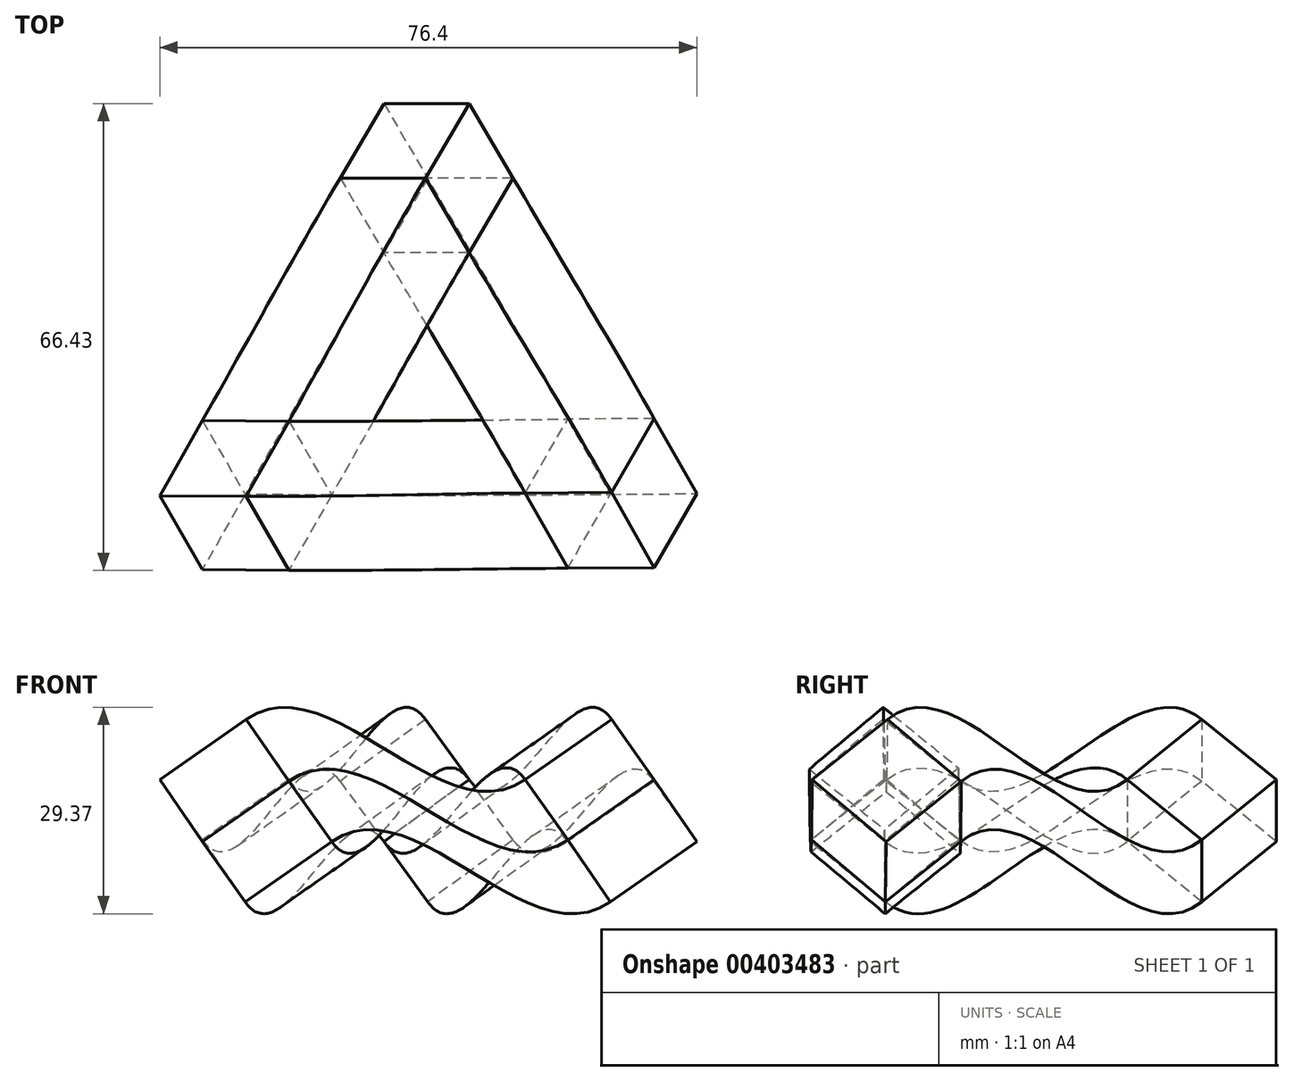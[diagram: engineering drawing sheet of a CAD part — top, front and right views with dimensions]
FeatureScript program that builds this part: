
annotation { "Feature Type Name" : "Feature", "Feature Type Description" : "" }
export const myFeature = defineFeature(function(context is Context, id is Id, definition is map)
    precondition{}
    {
        {
            var Q0;
            Q0=qCreatedBy(makeId("Top.planeOp"),FACE);
            var sketch = newSketch(context, id + "F0", { "sketchPlane" : qUnion([Q0])});
            skLineSegment(sketch, "E0", {"start": v(0, 0) * mm, "end": v(0, 80) * mm, "construction": true});
            skLineSegment(sketch, "E1", {"start": v(0, 0) * mm, "end": v(69.28, -40) * mm, "construction": true});
            skLineSegment(sketch, "E2", {"start": v(0, 0) * mm, "end": v(-69.28, -40) * mm, "construction": true});
            skSolve(sketch);
        }
        {
            var Q0;
            Q0=sQuery(id+"F0.wireOp",EDGE,"E0");
            cPlane(context, id + "F1", {"entities" : qUnion([Q0]), "cplaneType" : CPlaneType.LINE_ANGLE, "offset" : 25 * mm, "angle" : 54 * degree, "width" : 150 * mm, "height" : 150 * mm});
        }
        {
            var Q0;
            Q0=qCreatedBy(id+"F1.planeOp",FACE);
            var sketch = newSketch(context, id + "F2", { "sketchPlane" : qUnion([Q0])});
            skLineSegment(sketch, "E3.top", {"start": v(30, 0) * mm, "end": v(19.4, 10.6) * mm});
            skLineSegment(sketch, "E3.left", {"start": v(40.6, 10.6) * mm, "end": v(30, 0) * mm});
            skLineSegment(sketch, "E3.right", {"start": v(30, 21.21) * mm, "end": v(19.4, 10.6) * mm});
            skLineSegment(sketch, "E4", {"start": v(40.6, 10.6) * mm, "end": v(30, 21.21) * mm});
            skSolve(sketch);
        }
        {
            var Q0;
            Q0=sQuery(id+"F0.wireOp",EDGE,"E2");
            cPlane(context, id + "F3", {"entities" : qUnion([Q0]), "cplaneType" : CPlaneType.LINE_ANGLE, "offset" : 25 * mm, "angle" : 36 * degree, "oppositeDirection" : true, "width" : 150 * mm, "height" : 150 * mm});
        }
        {
            var Q0;
            Q0=qCreatedBy(id+"F3.planeOp",FACE);
            var sketch = newSketch(context, id + "F4", { "sketchPlane" : qUnion([Q0])});
            skLineSegment(sketch, "E5.0", {"start": v(0, 0) * mm, "end": v(-75.76, 25.7) * mm, "construction": true});
            skLineSegment(sketch, "E6", {"start": v(-14.96, 16.28) * mm, "end": v(-28.4, 9.64) * mm});
            skLineSegment(sketch, "E7", {"start": v(-14.96, 16.28) * mm, "end": v(-21.6, 29.73) * mm});
            skLineSegment(sketch, "E8", {"start": v(-35.04, 23.1) * mm, "end": v(-21.6, 29.73) * mm});
            skLineSegment(sketch, "E9", {"start": v(-28.4, 9.64) * mm, "end": v(-35.04, 23.1) * mm});
            skSolve(sketch);
        }
        {
            var Q0;
            Q0=sQuery(id+"F0.wireOp",EDGE,"E1");
            cPlane(context, id + "F5", {"entities" : qUnion([Q0]), "cplaneType" : CPlaneType.LINE_ANGLE, "offset" : 25 * mm, "angle" : 36 * degree, "oppositeDirection" : true, "width" : 150 * mm, "height" : 150 * mm});
        }
        {
            var Q0;
            Q0=qCreatedBy(id+"F5.planeOp",FACE);
            var sketch = newSketch(context, id + "F6", { "sketchPlane" : qUnion([Q0])});
            skLineSegment(sketch, "E10.0", {"start": v(0, 0) * mm, "end": v(-75.76, -25.7) * mm, "construction": true});
            skLineSegment(sketch, "E11", {"start": v(-28.4, -9.64) * mm, "end": v(-41.86, -3) * mm});
            skLineSegment(sketch, "E12", {"start": v(-41.86, -3) * mm, "end": v(-35.23, 10.45) * mm});
            skLineSegment(sketch, "E13", {"start": v(-35.23, 10.45) * mm, "end": v(-21.77, 3.81) * mm});
            skLineSegment(sketch, "E14", {"start": v(-21.77, 3.81) * mm, "end": v(-28.4, -9.64) * mm});
            skSolve(sketch);
        }
        {
            var Q0;
            Q0=makeQuery(id+"F2.imprint","IMPRINT",FACE,{"disambiguationData":[TD([[makeQuery(id+"F2.imprint","IMPRINT",EDGE,{"derivedFrom":sQuery(id+"F2.wireOp",EDGE,"E3.top")}),-1.0]])]});
            extrude(context, id + "F7", {"entities" : qUnion([Q0]), "depth" : 15 * mm});
        }
        {
            var Q0;
            Q0=makeQuery(id+"F4.imprint","IMPRINT",FACE,{"disambiguationData":[TD([[makeQuery(id+"F4.imprint","IMPRINT",EDGE,{"derivedFrom":sQuery(id+"F4.wireOp",EDGE,"E6")}),-1.0]])]});
            extrude(context, id + "F8", {"entities" : qUnion([Q0]), "oppositeDirection" : true, "depth" : 15 * mm});
        }
        {
            var Q0;
            Q0=makeQuery(id+"F6.imprint","IMPRINT",FACE,{"disambiguationData":[TD([[makeQuery(id+"F6.imprint","IMPRINT",EDGE,{"derivedFrom":sQuery(id+"F6.wireOp",EDGE,"E11")}),-1.0]])]});
            extrude(context, id + "F9", {"entities" : qUnion([Q0]), "oppositeDirection" : true, "depth" : 15 * mm});
        }
        {
            var Q0;
            Q0=makeQuery(id+"F7.opExtrude","SWEPT_FACE",FACE,{"disambiguationData":[OSD([sQuery(id+"F2.wireOp",EDGE,"E3.right")])]});
            var Q1;
            Q1=makeQuery(id+"F8.opExtrude","SWEPT_FACE",FACE,{"disambiguationData":[OSD([sQuery(id+"F4.wireOp",EDGE,"E6")])]});
            loft(context, id + "F10", {"startCondition" : LoftEndDerivativeType.NORMAL_TO_PROFILE, "startMagnitude" : 1.5, "endCondition" : LoftEndDerivativeType.NORMAL_TO_PROFILE, "endMagnitude" : 1.5, "sheetProfilesArray" : [{ "sheetProfileEntities" : qUnion([Q0]) }, { "sheetProfileEntities" : qUnion([Q1]) }]});
        }
        {
            var Q0;
            Q0=makeQuery(id+"F8.opExtrude","SWEPT_FACE",FACE,{"disambiguationData":[OSD([sQuery(id+"F4.wireOp",EDGE,"E7")])]});
            var Q1;
            Q1=makeQuery(id+"F9.opExtrude","SWEPT_FACE",FACE,{"disambiguationData":[OSD([sQuery(id+"F6.wireOp",EDGE,"E14")])]});
            loft(context, id + "F11", {"startCondition" : LoftEndDerivativeType.NORMAL_TO_PROFILE, "startMagnitude" : 1.5, "endCondition" : LoftEndDerivativeType.NORMAL_TO_PROFILE, "endMagnitude" : 1.5, "sheetProfilesArray" : [{ "sheetProfileEntities" : qUnion([Q0]) }, { "sheetProfileEntities" : qUnion([Q1]) }]});
        }
        {
            var Q0;
            Q0=makeQuery(id+"F9.opExtrude","SWEPT_FACE",FACE,{"disambiguationData":[OSD([sQuery(id+"F6.wireOp",EDGE,"E13")])]});
            var Q1;
            Q1=makeQuery(id+"F7.opExtrude","SWEPT_FACE",FACE,{"disambiguationData":[OSD([sQuery(id+"F2.wireOp",EDGE,"E3.top")])]});
            loft(context, id + "F12", {"startCondition" : LoftEndDerivativeType.NORMAL_TO_PROFILE, "startMagnitude" : 1.5, "endCondition" : LoftEndDerivativeType.NORMAL_TO_PROFILE, "endMagnitude" : 1.5, "sheetProfilesArray" : [{ "sheetProfileEntities" : qUnion([Q0]) }, { "sheetProfileEntities" : qUnion([Q1]) }]});
        }
    });
